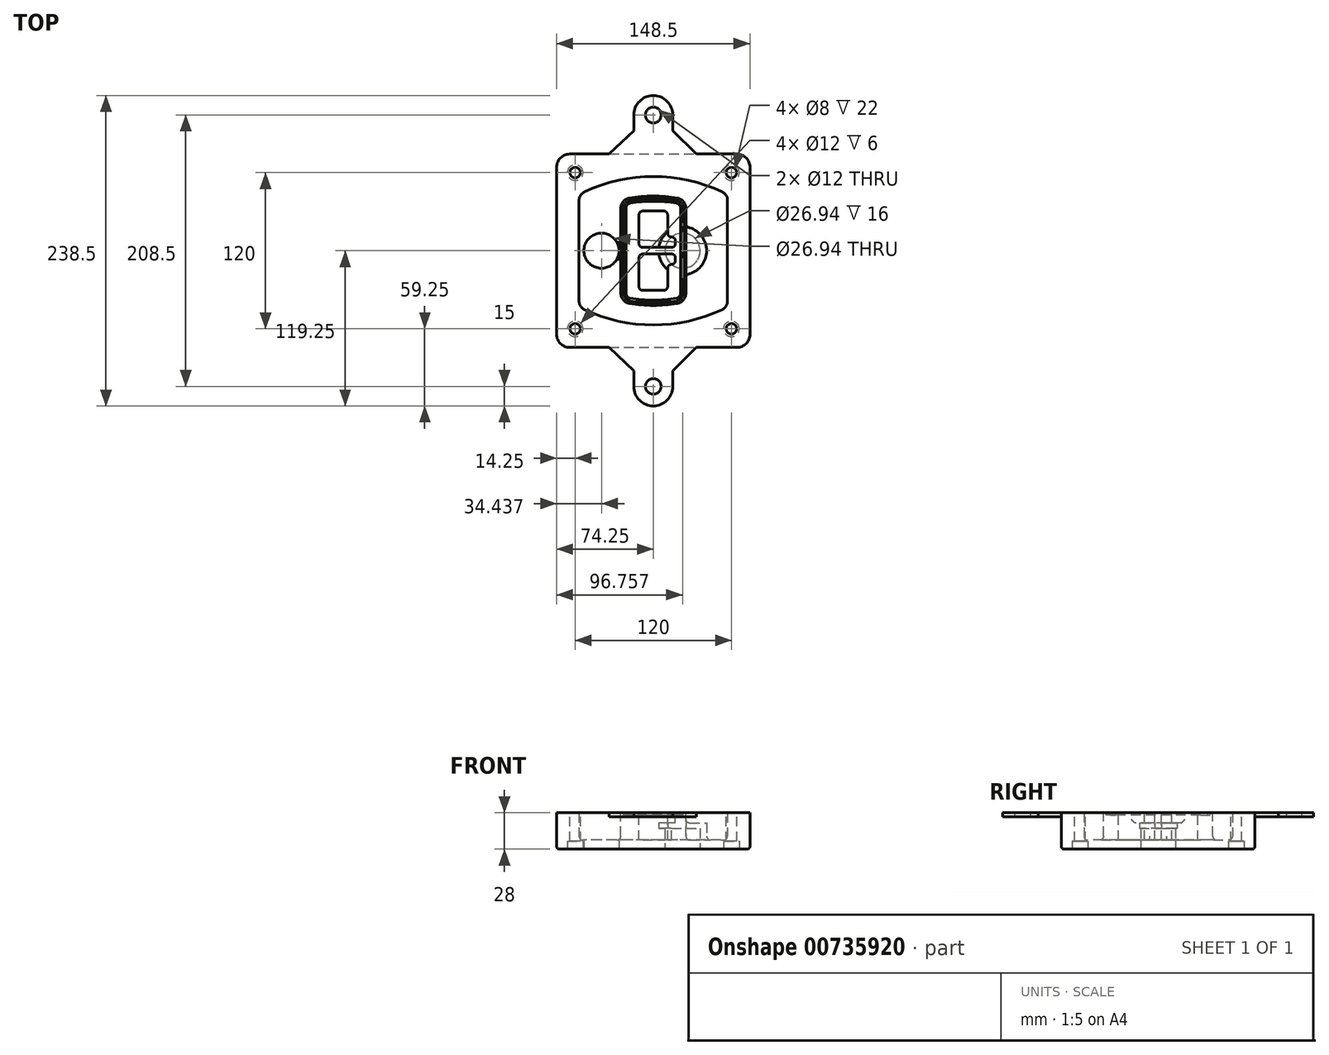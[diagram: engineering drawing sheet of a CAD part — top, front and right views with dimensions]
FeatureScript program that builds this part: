
annotation { "Feature Type Name" : "Feature", "Feature Type Description" : "" }
export const myFeature = defineFeature(function(context is Context, id is Id, definition is map)
    precondition{}
    {
        {
            var Q0;
            Q0=qCreatedBy(makeId("Top.planeOp"),FACE);
            var sketch = newSketch(context, id + "F0", { "sketchPlane" : qUnion([Q0])});
            skPoint(sketch, "E0.rect.middle", {"position": v(0, 0) * mm});
            skLineSegment(sketch, "E1.bottom", {"start": v(-64.25, -74.25) * mm, "end": v(64.25, -74.25) * mm});
            skLineSegment(sketch, "E1.top", {"start": v(-64.25, 74.25) * mm, "end": v(64.25, 74.25) * mm});
            skLineSegment(sketch, "E1.left", {"start": v(-74.25, -64.25) * mm, "end": v(-74.25, 64.25) * mm});
            skLineSegment(sketch, "E1.right", {"start": v(74.25, -64.25) * mm, "end": v(74.25, 64.25) * mm});
            skLineSegment(sketch, "E2", {"start": v(-74.25, 74.25) * mm, "end": v(74.25, -74.25) * mm, "construction": true});
            skLineSegment(sketch, "E3", {"start": v(74.25, 74.25) * mm, "end": v(-74.25, -74.25) * mm, "construction": true});
            skCircle(sketch, "E4", {"center": v(-60, 60) * mm, "radius": 4 * mm});
            skCircle(sketch, "E5", {"center": v(60, 60) * mm, "radius": 4 * mm});
            skCircle(sketch, "E6", {"center": v(60, -60) * mm, "radius": 4 * mm});
            skCircle(sketch, "E7", {"center": v(-60, -60) * mm, "radius": 4 * mm});
            skLineSegment(sketch, "E8", {"start": v(-60, 60) * mm, "end": v(60, 60) * mm, "construction": true});
            skLineSegment(sketch, "E9", {"start": v(60, 60) * mm, "end": v(60, -60) * mm, "construction": true});
            skLineSegment(sketch, "E10", {"start": v(60, -60) * mm, "end": v(-60, -60) * mm, "construction": true});
            skLineSegment(sketch, "E11", {"start": v(-60, -60) * mm, "end": v(-60, 60) * mm, "construction": true});
            skLineSegment(sketch, "E12", {"start": v(-60, 38.83) * mm, "end": v(-60, -38.83) * mm});
            skLineSegment(sketch, "E13", {"start": v(60, 38.83) * mm, "end": v(60, -38.83) * mm});
            skArc(sketch, "E14", {"start": v(54.26, 47.88) * mm, "mid": v(0, 60) * mm, "end": v(-54.26, 47.88) * mm});
            skArc(sketch, "E15", {"start": v(-54.26, -47.88) * mm, "mid": v(0, -60) * mm, "end": v(54.26, -47.88) * mm});
            skLineSegment(sketch, "E16", {"start": v(-60, 0) * mm, "end": v(60, 0) * mm, "construction": true});
            skPoint(sketch, "E17.visualSharp", {"position": v(-60, -45) * mm});
            skArc(sketch, "E17.filletArc", {"start": v(-60, -38.83) * mm, "mid": v(-58.44, -44.2) * mm, "end": v(-54.26, -47.88) * mm});
            skPoint(sketch, "E18.visualSharp", {"position": v(-60, 45) * mm});
            skArc(sketch, "E18.filletArc", {"start": v(-54.26, 47.88) * mm, "mid": v(-58.44, 44.2) * mm, "end": v(-60, 38.83) * mm});
            skPoint(sketch, "E19.visualSharp", {"position": v(60, 45) * mm});
            skArc(sketch, "E19.filletArc", {"start": v(60, 38.83) * mm, "mid": v(58.44, 44.2) * mm, "end": v(54.26, 47.88) * mm});
            skPoint(sketch, "E20.visualSharp", {"position": v(60, -45) * mm});
            skArc(sketch, "E20.filletArc", {"start": v(54.26, -47.88) * mm, "mid": v(58.44, -44.2) * mm, "end": v(60, -38.83) * mm});
            skPoint(sketch, "E21.visualSharp", {"position": v(-74.25, 74.25) * mm});
            skArc(sketch, "E21.filletArc", {"start": v(-64.25, 74.25) * mm, "mid": v(-71.32, 71.32) * mm, "end": v(-74.25, 64.25) * mm});
            skPoint(sketch, "E22.visualSharp", {"position": v(74.25, 74.25) * mm});
            skArc(sketch, "E22.filletArc", {"start": v(74.25, 64.25) * mm, "mid": v(71.32, 71.32) * mm, "end": v(64.25, 74.25) * mm});
            skPoint(sketch, "E23.visualSharp", {"position": v(74.25, -74.25) * mm});
            skArc(sketch, "E23.filletArc", {"start": v(64.25, -74.25) * mm, "mid": v(71.32, -71.32) * mm, "end": v(74.25, -64.25) * mm});
            skPoint(sketch, "E24.visualSharp", {"position": v(-74.25, -74.25) * mm});
            skArc(sketch, "E24.filletArc", {"start": v(-74.25, -64.25) * mm, "mid": v(-71.32, -71.32) * mm, "end": v(-64.25, -74.25) * mm});
            skArc(sketch, "E25.0", {"start": v(57, 38.83) * mm, "mid": v(55.9, 42.58) * mm, "end": v(52.98, 45.17) * mm});
            skLineSegment(sketch, "E25.1", {"start": v(57, 38.83) * mm, "end": v(57, -38.83) * mm});
            skArc(sketch, "E25.2", {"start": v(52.98, -45.17) * mm, "mid": v(55.9, -42.58) * mm, "end": v(57, -38.83) * mm});
            skArc(sketch, "E25.3", {"start": v(-52.98, -45.17) * mm, "mid": v(0, -57) * mm, "end": v(52.98, -45.17) * mm});
            skArc(sketch, "E25.4", {"start": v(-57, -38.83) * mm, "mid": v(-55.9, -42.58) * mm, "end": v(-52.98, -45.17) * mm});
            skArc(sketch, "E25.5", {"start": v(52.98, 45.17) * mm, "mid": v(0, 57) * mm, "end": v(-52.98, 45.17) * mm});
            skLineSegment(sketch, "E25.6", {"start": v(-57, 38.83) * mm, "end": v(-57, -38.83) * mm});
            skArc(sketch, "E25.7", {"start": v(-52.98, 45.17) * mm, "mid": v(-55.9, 42.58) * mm, "end": v(-57, 38.83) * mm});
            skArc(sketch, "E26.0", {"start": v(-55.96, 51.5) * mm, "mid": v(-61.82, 46.33) * mm, "end": v(-64, 38.83) * mm});
            skArc(sketch, "E26.1", {"start": v(55.96, 51.5) * mm, "mid": v(0, 64) * mm, "end": v(-55.96, 51.5) * mm});
            skArc(sketch, "E26.2", {"start": v(64, 38.83) * mm, "mid": v(61.82, 46.33) * mm, "end": v(55.96, 51.5) * mm});
            skLineSegment(sketch, "E26.3", {"start": v(64, 38.83) * mm, "end": v(64, -38.83) * mm});
            skArc(sketch, "E26.4", {"start": v(55.96, -51.5) * mm, "mid": v(61.82, -46.33) * mm, "end": v(64, -38.83) * mm});
            skLineSegment(sketch, "E26.5", {"start": v(-64, 38.83) * mm, "end": v(-64, -38.83) * mm});
            skArc(sketch, "E26.6", {"start": v(-55.96, -51.5) * mm, "mid": v(0, -64) * mm, "end": v(55.96, -51.5) * mm});
            skArc(sketch, "E26.7", {"start": v(-64, -38.83) * mm, "mid": v(-61.82, -46.33) * mm, "end": v(-55.96, -51.5) * mm});
            skSolve(sketch);
        }
        {
            var Q0;
            Q0=makeQuery(id+"F0.imprint","IMPRINT",FACE,{"disambiguationData":[TD([[makeQuery(id+"F0.imprint","IMPRINT",EDGE,{"derivedFrom":sQuery(id+"F0.wireOp",EDGE,"E1.bottom")}),1.0]])]});
            var Q1;
            Q1=makeQuery(id+"F0.imprint","IMPRINT",FACE,{"disambiguationData":[TD([[makeQuery(id+"F0.imprint","IMPRINT",EDGE,{"derivedFrom":sQuery(id+"F0.wireOp",EDGE,"E12")}),1.0]])]});
            var Q2;
            Q2=makeQuery(id+"F0.imprint","IMPRINT",FACE,{"disambiguationData":[TD([[makeQuery(id+"F0.imprint","IMPRINT",EDGE,{"derivedFrom":sQuery(id+"F0.wireOp",EDGE,"E25.0")}),1.0]])]});
            var Q3;
            Q3=makeQuery(id+"F0.imprint","IMPRINT",FACE,{"disambiguationData":[TD([[makeQuery(id+"F0.imprint","IMPRINT",EDGE,{"derivedFrom":sQuery(id+"F0.wireOp",EDGE,"E12")}),-1.0]])]});
            extrude(context, id + "F1", {"entities" : qUnion([Q0, Q1, Q2, Q3]), "oppositeDirection" : true, "depth" : 25 * mm});
        }
        {
            var Q0;
            Q0=makeQuery(id+"F0.imprint","IMPRINT",FACE,{"disambiguationData":[TD([[makeQuery(id+"F0.imprint","IMPRINT",EDGE,{"derivedFrom":sQuery(id+"F0.wireOp",EDGE,"E12")}),1.0]])]});
            extrude(context, id + "F2", {"entities" : qUnion([Q0]), "operationType" : NewBodyOperationType.ADD, "depth" : 3 * mm});
        }
        {
            var Q0;
            Q0=makeQuery(id+"F0.imprint","IMPRINT",FACE,{"disambiguationData":[TD([[makeQuery(id+"F0.imprint","IMPRINT",EDGE,{"derivedFrom":sQuery(id+"F0.wireOp",EDGE,"E25.0")}),1.0]])]});
            extrude(context, id + "F3", {"entities" : qUnion([Q0]), "operationType" : NewBodyOperationType.REMOVE, "oppositeDirection" : true, "depth" : 18 * mm});
        }
        {
            var Q0;
            Q0=makeQuery(id+"F2.opExtrude","CAP_FACE",FACE,{"disambiguationData":[OSD([sQuery(id+"F0.wireOp",EDGE,"E12"),sQuery(id+"F0.wireOp",EDGE,"E13"),sQuery(id+"F0.wireOp",EDGE,"E14"),sQuery(id+"F0.wireOp",EDGE,"E15"),sQuery(id+"F0.wireOp",EDGE,"E17.filletArc"),sQuery(id+"F0.wireOp",EDGE,"E18.filletArc"),sQuery(id+"F0.wireOp",EDGE,"E19.filletArc"),sQuery(id+"F0.wireOp",EDGE,"E20.filletArc"),sQuery(id+"F0.wireOp",EDGE,"E25.0"),sQuery(id+"F0.wireOp",EDGE,"E25.1"),sQuery(id+"F0.wireOp",EDGE,"E25.2"),sQuery(id+"F0.wireOp",EDGE,"E25.3"),sQuery(id+"F0.wireOp",EDGE,"E25.4"),sQuery(id+"F0.wireOp",EDGE,"E25.5"),sQuery(id+"F0.wireOp",EDGE,"E25.6"),sQuery(id+"F0.wireOp",EDGE,"E25.7")])],"isStart":false});
            var sketch = newSketch(context, id + "F4", { "sketchPlane" : qUnion([Q0])});
            skArc(sketch, "E27.0", {"start": v(-18.34, -40.45) * mm, "mid": v(0, -42) * mm, "end": v(18.34, -40.45) * mm});
            skArc(sketch, "E28.0", {"start": v(18.34, 40.45) * mm, "mid": v(0, 42) * mm, "end": v(-18.34, 40.45) * mm});
            skLineSegment(sketch, "E29", {"start": v(-25, 32.57) * mm, "end": v(-25, -32.57) * mm});
            skLineSegment(sketch, "E30", {"start": v(25, 32.57) * mm, "end": v(25, -32.57) * mm});
            skLineSegment(sketch, "E31", {"start": v(-25, 39.1) * mm, "end": v(25, 39.1) * mm, "construction": true});
            skLineSegment(sketch, "E32", {"start": v(-25, -39.1) * mm, "end": v(25, -39.1) * mm, "construction": true});
            skPoint(sketch, "E33.visualSharp", {"position": v(-25, 39.1) * mm});
            skArc(sketch, "E33.filletArc", {"start": v(-18.34, 40.45) * mm, "mid": v(-23.11, 37.73) * mm, "end": v(-25, 32.57) * mm});
            skPoint(sketch, "E34.visualSharp", {"position": v(25, 39.1) * mm});
            skArc(sketch, "E34.filletArc", {"start": v(25, 32.57) * mm, "mid": v(23.11, 37.73) * mm, "end": v(18.34, 40.45) * mm});
            skPoint(sketch, "E35.visualSharp", {"position": v(25, -39.1) * mm});
            skArc(sketch, "E35.filletArc", {"start": v(18.34, -40.45) * mm, "mid": v(23.11, -37.73) * mm, "end": v(25, -32.57) * mm});
            skPoint(sketch, "E36.visualSharp", {"position": v(-25, -39.1) * mm});
            skArc(sketch, "E36.filletArc", {"start": v(-25, -32.57) * mm, "mid": v(-23.11, -37.73) * mm, "end": v(-18.34, -40.45) * mm});
            skArc(sketch, "E37.0", {"start": v(52.98, 45.17) * mm, "mid": v(0, 57) * mm, "end": v(-52.98, 45.17) * mm});
            skArc(sketch, "E37.1", {"start": v(-52.98, 45.17) * mm, "mid": v(-55.9, 42.58) * mm, "end": v(-57, 38.83) * mm});
            skLineSegment(sketch, "E37.2", {"start": v(-57, 38.83) * mm, "end": v(-57, -38.83) * mm});
            skArc(sketch, "E37.3", {"start": v(-57, -38.83) * mm, "mid": v(-55.9, -42.58) * mm, "end": v(-52.98, -45.17) * mm});
            skArc(sketch, "E37.4", {"start": v(-52.98, -45.17) * mm, "mid": v(0, -57) * mm, "end": v(52.98, -45.17) * mm});
            skArc(sketch, "E37.5", {"start": v(52.98, -45.17) * mm, "mid": v(55.9, -42.58) * mm, "end": v(57, -38.83) * mm});
            skLineSegment(sketch, "E37.6", {"start": v(57, 38.83) * mm, "end": v(57, -38.83) * mm});
            skArc(sketch, "E37.7", {"start": v(57, 38.83) * mm, "mid": v(55.9, 42.58) * mm, "end": v(52.98, 45.17) * mm});
            skLineSegment(sketch, "E38.0", {"start": v(23, 32.57) * mm, "end": v(23, -32.57) * mm});
            skArc(sketch, "E38.1", {"start": v(18, -38.48) * mm, "mid": v(21.58, -36.44) * mm, "end": v(23, -32.57) * mm});
            skArc(sketch, "E38.2", {"start": v(-18, -38.48) * mm, "mid": v(0, -40) * mm, "end": v(18, -38.48) * mm});
            skArc(sketch, "E38.3", {"start": v(-23, -32.57) * mm, "mid": v(-21.58, -36.44) * mm, "end": v(-18, -38.48) * mm});
            skLineSegment(sketch, "E38.4", {"start": v(-23, 32.57) * mm, "end": v(-23, -32.57) * mm});
            skArc(sketch, "E38.5", {"start": v(23, 32.57) * mm, "mid": v(21.58, 36.44) * mm, "end": v(18, 38.48) * mm});
            skArc(sketch, "E38.6", {"start": v(-18, 38.48) * mm, "mid": v(-21.58, 36.44) * mm, "end": v(-23, 32.57) * mm});
            skArc(sketch, "E38.7", {"start": v(18, 38.48) * mm, "mid": v(0, 40) * mm, "end": v(-18, 38.48) * mm});
            skArc(sketch, "E39.0", {"start": v(21, 32.57) * mm, "mid": v(20.06, 35.15) * mm, "end": v(17.67, 36.5) * mm});
            skLineSegment(sketch, "E39.1", {"start": v(21, 32.57) * mm, "end": v(21, -32.57) * mm});
            skArc(sketch, "E39.2", {"start": v(17.67, -36.5) * mm, "mid": v(20.06, -35.15) * mm, "end": v(21, -32.57) * mm});
            skArc(sketch, "E39.3", {"start": v(-17.67, -36.5) * mm, "mid": v(0, -38) * mm, "end": v(17.67, -36.5) * mm});
            skArc(sketch, "E39.4", {"start": v(-21, -32.57) * mm, "mid": v(-20.06, -35.15) * mm, "end": v(-17.67, -36.5) * mm});
            skArc(sketch, "E39.5", {"start": v(17.67, 36.5) * mm, "mid": v(0, 38) * mm, "end": v(-17.67, 36.5) * mm});
            skLineSegment(sketch, "E39.6", {"start": v(-21, 32.57) * mm, "end": v(-21, -32.57) * mm});
            skArc(sketch, "E39.7", {"start": v(-17.67, 36.5) * mm, "mid": v(-20.06, 35.15) * mm, "end": v(-21, 32.57) * mm});
            skLineSegment(sketch, "E40", {"start": v(-25, 0) * mm, "end": v(25, 0) * mm, "construction": true});
            skLineSegment(sketch, "E41", {"start": v(-11, 5.5) * mm, "end": v(-11, 27.5) * mm});
            skLineSegment(sketch, "E42", {"start": v(-8, 30.5) * mm, "end": v(8, 30.5) * mm});
            skLineSegment(sketch, "E43", {"start": v(11, 27.5) * mm, "end": v(11, 13.5) * mm});
            skLineSegment(sketch, "E44", {"start": v(14, 10.5) * mm, "end": v(14, 10.5) * mm});
            skLineSegment(sketch, "E45", {"start": v(17, 7.5) * mm, "end": v(17, 5.5) * mm});
            skLineSegment(sketch, "E46", {"start": v(14, 2.5) * mm, "end": v(-8, 2.5) * mm});
            skPoint(sketch, "E47.visualSharp", {"position": v(-11, 30.5) * mm});
            skArc(sketch, "E47.filletArc", {"start": v(-8, 30.5) * mm, "mid": v(-10.12, 29.62) * mm, "end": v(-11, 27.5) * mm});
            skPoint(sketch, "E48.visualSharp", {"position": v(11, 30.5) * mm});
            skArc(sketch, "E48.filletArc", {"start": v(11, 27.5) * mm, "mid": v(10.12, 29.62) * mm, "end": v(8, 30.5) * mm});
            skPoint(sketch, "E49.visualSharp", {"position": v(11, 10.5) * mm});
            skArc(sketch, "E49.filletArc", {"start": v(11, 13.5) * mm, "mid": v(11.88, 11.38) * mm, "end": v(14, 10.5) * mm});
            skPoint(sketch, "E50.visualSharp", {"position": v(17, 10.5) * mm});
            skArc(sketch, "E50.filletArc", {"start": v(17, 7.5) * mm, "mid": v(16.12, 9.62) * mm, "end": v(14, 10.5) * mm});
            skPoint(sketch, "E51.visualSharp", {"position": v(17, 2.5) * mm});
            skArc(sketch, "E51.filletArc", {"start": v(14, 2.5) * mm, "mid": v(16.12, 3.38) * mm, "end": v(17, 5.5) * mm});
            skPoint(sketch, "E52.visualSharp", {"position": v(-11, 2.5) * mm});
            skArc(sketch, "E52.filletArc", {"start": v(-11, 5.5) * mm, "mid": v(-10.12, 3.38) * mm, "end": v(-8, 2.5) * mm});
            skLineSegment(sketch, "E53.0.MirrorCS", {"start": v(14, -2.5) * mm, "end": v(-8, -2.5) * mm});
            skArc(sketch, "E54.0.MirrorCS", {"start": v(-11, -5.5) * mm, "mid": v(-10.12, -3.38) * mm, "end": v(-8, -2.5) * mm});
            skLineSegment(sketch, "E55.0.MirrorCS", {"start": v(-11, -5.5) * mm, "end": v(-11, -27.5) * mm});
            skArc(sketch, "E56.0.MirrorCS", {"start": v(-8, -30.5) * mm, "mid": v(-10.12, -29.62) * mm, "end": v(-11, -27.5) * mm});
            skLineSegment(sketch, "E57.0.MirrorCS", {"start": v(-8, -30.5) * mm, "end": v(8, -30.5) * mm});
            skArc(sketch, "E58.0.MirrorCS", {"start": v(11, -27.5) * mm, "mid": v(10.12, -29.62) * mm, "end": v(8, -30.5) * mm});
            skLineSegment(sketch, "E59.0.MirrorCS", {"start": v(11, -27.5) * mm, "end": v(11, -13.5) * mm});
            skArc(sketch, "E60.0.MirrorCS", {"start": v(11, -13.5) * mm, "mid": v(11.88, -11.38) * mm, "end": v(14, -10.5) * mm});
            skArc(sketch, "E61.0.MirrorCS", {"start": v(17, -7.5) * mm, "mid": v(16.12, -9.62) * mm, "end": v(14, -10.5) * mm});
            skLineSegment(sketch, "E62.0.MirrorCS", {"start": v(17, -7.5) * mm, "end": v(17, -5.5) * mm});
            skArc(sketch, "E63.0.MirrorCS", {"start": v(14, -2.5) * mm, "mid": v(16.12, -3.38) * mm, "end": v(17, -5.5) * mm});
            skSolve(sketch);
        }
        {
            var Q0;
            Q0=makeQuery(id+"F4.imprint","IMPRINT",FACE,{"disambiguationData":[TD([[makeQuery(id+"F4.imprint","IMPRINT",EDGE,{"derivedFrom":sQuery(id+"F4.wireOp",EDGE,"E27.0")}),1.0]])]});
            var Q1;
            Q1=makeQuery(id+"F4.imprint","IMPRINT",FACE,{"disambiguationData":[TD([[makeQuery(id+"F4.imprint","IMPRINT",EDGE,{"derivedFrom":sQuery(id+"F4.wireOp",EDGE,"E38.0")}),-1.0]])]});
            var Q2;
            Q2=makeQuery(id+"F4.imprint","IMPRINT",FACE,{"disambiguationData":[TD([[makeQuery(id+"F4.imprint","IMPRINT",EDGE,{"derivedFrom":sQuery(id+"F4.wireOp",EDGE,"E39.0")}),1.0]])]});
            extrude(context, id + "F5", {"entities" : qUnion([Q0, Q1, Q2]), "operationType" : NewBodyOperationType.ADD, "endBound" : BoundingType.UP_TO_NEXT, "oppositeDirection" : true, "depth" : 25 * mm});
        }
        {
            var Q0;
            Q0=makeQuery(id+"F4.imprint","IMPRINT",FACE,{"disambiguationData":[TD([[makeQuery(id+"F4.imprint","IMPRINT",EDGE,{"derivedFrom":sQuery(id+"F4.wireOp",EDGE,"E38.0")}),-1.0]])]});
            extrude(context, id + "F6", {"entities" : qUnion([Q0]), "operationType" : NewBodyOperationType.REMOVE, "oppositeDirection" : true, "depth" : 2 * mm});
        }
        {
            var Q0;
            Q0=makeQuery(id+"F1.opExtrude","CAP_FACE",FACE,{"disambiguationData":[OSD([sQuery(id+"F0.wireOp",EDGE,"E1.bottom"),sQuery(id+"F0.wireOp",EDGE,"E1.top"),sQuery(id+"F0.wireOp",EDGE,"E1.left"),sQuery(id+"F0.wireOp",EDGE,"E1.right"),sQuery(id+"F0.wireOp",EDGE,"E4"),sQuery(id+"F0.wireOp",EDGE,"E5"),sQuery(id+"F0.wireOp",EDGE,"E6"),sQuery(id+"F0.wireOp",EDGE,"E7"),sQuery(id+"F0.wireOp",EDGE,"E21.filletArc"),sQuery(id+"F0.wireOp",EDGE,"E22.filletArc"),sQuery(id+"F0.wireOp",EDGE,"E23.filletArc"),sQuery(id+"F0.wireOp",EDGE,"E24.filletArc")])],"isStart":false});
            var sketch = newSketch(context, id + "F7", { "sketchPlane" : qUnion([Q0])});
            skCircle(sketch, "E64", {"center": v(22.5, 0) * mm, "radius": 13.47 * mm});
            skCircle(sketch, "E65", {"center": v(-39.81, 0) * mm, "radius": 13.47 * mm});
            skLineSegment(sketch, "E66", {"start": v(74.25, 0) * mm, "end": v(-74.25, 0) * mm});
            skCircle(sketch, "E67", {"center": v(22.5, 0) * mm, "radius": 18.47 * mm});
            skCircle(sketch, "E68", {"center": v(60, -60) * mm, "radius": 6 * mm});
            skCircle(sketch, "E69", {"center": v(-60, -60) * mm, "radius": 6 * mm});
            skCircle(sketch, "E70", {"center": v(-60, 60) * mm, "radius": 6 * mm});
            skCircle(sketch, "E71", {"center": v(60, 60) * mm, "radius": 6 * mm});
            skSolve(sketch);
        }
        {
            var Q0;
            {var subQ1=sQuery(id+"F7.wireOp",EDGE,"E66");var subQ4=sQuery(id+"F7.wireOp",EDGE,"E64");var subQ6=makeQuery(id+"F7.imprint","INTERSECT",VERTEX,{"disambiguationData":[OD(0.0)],"derivedFrom":[subQ4,subQ1]});Q0=makeQuery(id+"F7.imprint","IMPRINT",FACE,{"disambiguationData":[TD([[makeQuery(id+"F7.imprint","IMPRINT",EDGE,{"disambiguationData":[TD([[subQ6,-1.0]])],"derivedFrom":subQ4}),-1.0]])]});}
            var Q1;
            {var subQ0=sQuery(id+"F7.wireOp",EDGE,"E66");var subQ1=sQuery(id+"F7.wireOp",EDGE,"E64");var subQ3=makeQuery(id+"F7.imprint","INTERSECT",VERTEX,{"disambiguationData":[OD(0.0)],"derivedFrom":[subQ1,subQ0]});Q1=makeQuery(id+"F7.imprint","IMPRINT",FACE,{"disambiguationData":[TD([[makeQuery(id+"F7.imprint","IMPRINT",EDGE,{"disambiguationData":[TD([[subQ3,-1.0]])],"derivedFrom":subQ1}),1.0]])]});}
            var Q2;
            {var subQ0=sQuery(id+"F7.wireOp",EDGE,"E66");var subQ1=sQuery(id+"F7.wireOp",EDGE,"E64");var subQ3=makeQuery(id+"F7.imprint","INTERSECT",VERTEX,{"disambiguationData":[OD(0.0)],"derivedFrom":[subQ1,subQ0]});Q2=makeQuery(id+"F7.imprint","IMPRINT",FACE,{"disambiguationData":[TD([[makeQuery(id+"F7.imprint","IMPRINT",EDGE,{"disambiguationData":[TD([[subQ3,1.0]])],"derivedFrom":subQ1}),1.0]])]});}
            var Q3;
            {var subQ1=sQuery(id+"F7.wireOp",EDGE,"E66");var subQ4=sQuery(id+"F7.wireOp",EDGE,"E64");var subQ6=makeQuery(id+"F7.imprint","INTERSECT",VERTEX,{"disambiguationData":[OD(0.0)],"derivedFrom":[subQ4,subQ1]});Q3=makeQuery(id+"F7.imprint","IMPRINT",FACE,{"disambiguationData":[TD([[makeQuery(id+"F7.imprint","IMPRINT",EDGE,{"disambiguationData":[TD([[subQ6,1.0]])],"derivedFrom":subQ4}),-1.0]])]});}
            extrude(context, id + "F8", {"entities" : qUnion([Q0, Q1, Q2, Q3]), "operationType" : NewBodyOperationType.ADD, "oppositeDirection" : true, "depth" : 20 * mm});
        }
        {
            var Q0;
            {var subQ0=sQuery(id+"F7.wireOp",EDGE,"E66");var subQ1=sQuery(id+"F7.wireOp",EDGE,"E64");var subQ3=makeQuery(id+"F7.imprint","INTERSECT",VERTEX,{"disambiguationData":[OD(0.0)],"derivedFrom":[subQ1,subQ0]});Q0=makeQuery(id+"F7.imprint","IMPRINT",FACE,{"disambiguationData":[TD([[makeQuery(id+"F7.imprint","IMPRINT",EDGE,{"disambiguationData":[TD([[subQ3,-1.0]])],"derivedFrom":subQ1}),1.0]])]});}
            var Q1;
            {var subQ0=sQuery(id+"F7.wireOp",EDGE,"E66");var subQ1=sQuery(id+"F7.wireOp",EDGE,"E64");var subQ3=makeQuery(id+"F7.imprint","INTERSECT",VERTEX,{"disambiguationData":[OD(0.0)],"derivedFrom":[subQ1,subQ0]});Q1=makeQuery(id+"F7.imprint","IMPRINT",FACE,{"disambiguationData":[TD([[makeQuery(id+"F7.imprint","IMPRINT",EDGE,{"disambiguationData":[TD([[subQ3,1.0]])],"derivedFrom":subQ1}),1.0]])]});}
            extrude(context, id + "F9", {"entities" : qUnion([Q0, Q1]), "operationType" : NewBodyOperationType.REMOVE, "oppositeDirection" : true, "depth" : 16 * mm});
        }
        {
            var Q0;
            {var subQ0=sQuery(id+"F7.wireOp",EDGE,"E66");var subQ1=sQuery(id+"F7.wireOp",EDGE,"E65");var subQ3=makeQuery(id+"F7.imprint","INTERSECT",VERTEX,{"disambiguationData":[OD(0.0)],"derivedFrom":[subQ1,subQ0]});Q0=makeQuery(id+"F7.imprint","IMPRINT",FACE,{"disambiguationData":[TD([[makeQuery(id+"F7.imprint","IMPRINT",EDGE,{"disambiguationData":[TD([[subQ3,-1.0]])],"derivedFrom":subQ1}),1.0]])]});}
            var Q1;
            {var subQ0=sQuery(id+"F7.wireOp",EDGE,"E66");var subQ1=sQuery(id+"F7.wireOp",EDGE,"E65");var subQ3=makeQuery(id+"F7.imprint","INTERSECT",VERTEX,{"disambiguationData":[OD(0.0)],"derivedFrom":[subQ1,subQ0]});Q1=makeQuery(id+"F7.imprint","IMPRINT",FACE,{"disambiguationData":[TD([[makeQuery(id+"F7.imprint","IMPRINT",EDGE,{"disambiguationData":[TD([[subQ3,1.0]])],"derivedFrom":subQ1}),1.0]])]});}
            extrude(context, id + "F10", {"entities" : qUnion([Q0, Q1]), "operationType" : NewBodyOperationType.REMOVE, "oppositeDirection" : true, "depth" : 25 * mm});
        }
        {
            var Q0;
            Q0=makeQuery(id+"F7.imprint","IMPRINT",FACE,{"disambiguationData":[TD([[makeQuery(id+"F7.imprint","IMPRINT",EDGE,{"derivedFrom":sQuery(id+"F7.wireOp",EDGE,"E68")}),1.0]])]});
            var Q1;
            Q1=makeQuery(id+"F7.imprint","IMPRINT",FACE,{"disambiguationData":[TD([[makeQuery(id+"F7.imprint","IMPRINT",EDGE,{"derivedFrom":makeQuery(id+"F1.opExtrude","CAP_EDGE",EDGE,{"disambiguationData":[OSD([sQuery(id+"F0.wireOp",EDGE,"E5")])],"isStart":false})}),-1.0]])]});
            var Q2;
            Q2=makeQuery(id+"F7.imprint","IMPRINT",FACE,{"disambiguationData":[TD([[makeQuery(id+"F7.imprint","IMPRINT",EDGE,{"derivedFrom":sQuery(id+"F7.wireOp",EDGE,"E69")}),1.0]])]});
            var Q3;
            Q3=makeQuery(id+"F7.imprint","IMPRINT",FACE,{"disambiguationData":[TD([[makeQuery(id+"F7.imprint","IMPRINT",EDGE,{"derivedFrom":makeQuery(id+"F1.opExtrude","CAP_EDGE",EDGE,{"disambiguationData":[OSD([sQuery(id+"F0.wireOp",EDGE,"E4")])],"isStart":false})}),-1.0]])]});
            var Q4;
            Q4=makeQuery(id+"F7.imprint","IMPRINT",FACE,{"disambiguationData":[TD([[makeQuery(id+"F7.imprint","IMPRINT",EDGE,{"derivedFrom":sQuery(id+"F7.wireOp",EDGE,"E70")}),1.0]])]});
            var Q5;
            Q5=makeQuery(id+"F7.imprint","IMPRINT",FACE,{"disambiguationData":[TD([[makeQuery(id+"F7.imprint","IMPRINT",EDGE,{"derivedFrom":makeQuery(id+"F1.opExtrude","CAP_EDGE",EDGE,{"disambiguationData":[OSD([sQuery(id+"F0.wireOp",EDGE,"E7")])],"isStart":false})}),-1.0]])]});
            var Q6;
            Q6=makeQuery(id+"F7.imprint","IMPRINT",FACE,{"disambiguationData":[TD([[makeQuery(id+"F7.imprint","IMPRINT",EDGE,{"derivedFrom":sQuery(id+"F7.wireOp",EDGE,"E71")}),1.0]])]});
            var Q7;
            Q7=makeQuery(id+"F7.imprint","IMPRINT",FACE,{"disambiguationData":[TD([[makeQuery(id+"F7.imprint","IMPRINT",EDGE,{"derivedFrom":makeQuery(id+"F1.opExtrude","CAP_EDGE",EDGE,{"disambiguationData":[OSD([sQuery(id+"F0.wireOp",EDGE,"E6")])],"isStart":false})}),-1.0]])]});
            extrude(context, id + "F11", {"entities" : qUnion([Q0, Q1, Q2, Q3, Q4, Q5, Q6, Q7]), "operationType" : NewBodyOperationType.REMOVE, "oppositeDirection" : true, "depth" : 6 * mm});
        }
        {
            var Q0;
            Q0=makeQuery(id+"F9.boolean.opBoolean","COPY",FACE,{"derivedFrom":makeQuery(id+"F9.opExtrude","CAP_FACE",FACE,{"disambiguationData":[OSD([sQuery(id+"F7.wireOp",EDGE,"E64")])],"isStart":false})});
            var sketch = newSketch(context, id + "F12", { "sketchPlane" : qUnion([Q0])});
            skArc(sketch, "E72.0", {"start": v(11, 14.45) * mm, "mid": v(6.45, 9.13) * mm, "end": v(4.2, 2.5) * mm});
            skArc(sketch, "E72.1", {"start": v(4.2, -2.5) * mm, "mid": v(6.45, -9.13) * mm, "end": v(11, -14.45) * mm});
            skLineSegment(sketch, "E73", {"start": v(4.2, -2.5) * mm, "end": v(14, -2.5) * mm});
            skLineSegment(sketch, "E74.0", {"start": v(14, 2.5) * mm, "end": v(4.2, 2.5) * mm});
            skArc(sketch, "E74.1", {"start": v(14, 2.5) * mm, "mid": v(16.12, 3.38) * mm, "end": v(17, 5.5) * mm});
            skLineSegment(sketch, "E74.2", {"start": v(17, 7.5) * mm, "end": v(17, 5.5) * mm});
            skArc(sketch, "E74.3", {"start": v(17, 7.5) * mm, "mid": v(16.12, 9.62) * mm, "end": v(14, 10.5) * mm});
            skArc(sketch, "E74.4", {"start": v(11, 13.5) * mm, "mid": v(11.88, 11.38) * mm, "end": v(14, 10.5) * mm});
            skLineSegment(sketch, "E74.5", {"start": v(11, 14.45) * mm, "end": v(11, 13.5) * mm});
            skLineSegment(sketch, "E74.7", {"start": v(14, -2.5) * mm, "end": v(4.2, -2.5) * mm});
            skArc(sketch, "E74.8", {"start": v(14, -2.5) * mm, "mid": v(16.12, -3.38) * mm, "end": v(17, -5.5) * mm});
            skLineSegment(sketch, "E74.9", {"start": v(17, -7.5) * mm, "end": v(17, -5.5) * mm});
            skArc(sketch, "E74.10", {"start": v(17, -7.5) * mm, "mid": v(16.12, -9.62) * mm, "end": v(14, -10.5) * mm});
            skArc(sketch, "E74.11", {"start": v(11, -13.5) * mm, "mid": v(11.88, -11.38) * mm, "end": v(14, -10.5) * mm});
            skLineSegment(sketch, "E74.12", {"start": v(11, -14.45) * mm, "end": v(11, -13.5) * mm});
            skPoint(sketch, "E75.orphan", {"position": v(11, -27.5) * mm});
            skPoint(sketch, "E76.orphan", {"position": v(-8, -2.5) * mm});
            skPoint(sketch, "E77.orphan", {"position": v(-8, 2.5) * mm});
            skPoint(sketch, "E78.orphan", {"position": v(11, 27.5) * mm});
            skSolve(sketch);
        }
        {
            var Q0;
            {var subQ7=sQuery(id+"F12.wireOp",EDGE,"E72.0");var subQ14=sQuery(id+"F12.wireOp",EDGE,"E72.1");var subQ16=sQuery(id+"F12.wireOp",EDGE,"E74.1");var subQ18=sQuery(id+"F12.wireOp",EDGE,"E74.8");Q0=qUnion([makeQuery(id+"F12.imprint","IMPRINT",FACE,{"disambiguationData":[TD([[makeQuery(id+"F12.imprint","IMPRINT",EDGE,{"derivedFrom":subQ7}),1.0]])]}),makeQuery(id+"F12.imprint","IMPRINT",FACE,{"disambiguationData":[TD([[makeQuery(id+"F12.imprint","IMPRINT",EDGE,{"derivedFrom":subQ14}),1.0]])]}),makeQuery(id+"F12.imprint","IMPRINT",FACE,{"disambiguationData":[TD([[makeQuery(id+"F12.imprint","IMPRINT",EDGE,{"derivedFrom":subQ16}),1.0]])]}),makeQuery(id+"F12.imprint","IMPRINT",FACE,{"disambiguationData":[TD([[makeQuery(id+"F12.imprint","IMPRINT",EDGE,{"derivedFrom":subQ18}),-1.0]])]})]);}
            var Q1;
            Q1=makeQuery(id+"F5.boolean.opBoolean","SPLIT",FACE,{"disambiguationData":[TD([makeQuery(id+"F5.opExtrude","SWEPT_FACE",FACE,{"disambiguationData":[OSD([sQuery(id+"F4.wireOp",EDGE,"E41")])]})])],"derivedFrom":makeQuery(id+"F3.boolean.opBoolean","COPY",FACE,{"derivedFrom":makeQuery(id+"F3.opExtrude","CAP_FACE",FACE,{"disambiguationData":[OSD([sQuery(id+"F0.wireOp",EDGE,"E25.0"),sQuery(id+"F0.wireOp",EDGE,"E25.1"),sQuery(id+"F0.wireOp",EDGE,"E25.2"),sQuery(id+"F0.wireOp",EDGE,"E25.3"),sQuery(id+"F0.wireOp",EDGE,"E25.4"),sQuery(id+"F0.wireOp",EDGE,"E25.5"),sQuery(id+"F0.wireOp",EDGE,"E25.6"),sQuery(id+"F0.wireOp",EDGE,"E25.7")])],"isStart":false})})});
            extrude(context, id + "F13", {"entities" : qUnion([Q0]), "operationType" : NewBodyOperationType.REMOVE, "endBound" : BoundingType.UP_TO_SURFACE, "endBoundEntityFace" : qUnion([Q1]), "depth" : 25 * mm});
        }
        {
            var Q0;
            Q0=makeQuery(id+"F3.boolean.opBoolean","COPY",EDGE,{"derivedFrom":makeQuery(id+"F3.opExtrude","CAP_EDGE",EDGE,{"disambiguationData":[OSD([sQuery(id+"F0.wireOp",EDGE,"E25.6")])],"isStart":false})});
            var Q1;
            Q1=makeQuery(id+"F8.boolean.opBoolean","INTERSECT",EDGE,{"derivedFrom":[makeQuery(id+"F5.opExtrude","SWEPT_FACE",FACE,{"disambiguationData":[OSD([sQuery(id+"F4.wireOp",EDGE,"E30")])]}),makeQuery(id+"F8.opExtrude","CAP_FACE",FACE,{"disambiguationData":[OSD([sQuery(id+"F7.wireOp",EDGE,"E67")])],"isStart":false})]});
            var Q2;
            Q2=makeQuery(id+"F8.boolean.opBoolean","INTERSECT",EDGE,{"disambiguationData":[OD(1.0)],"derivedFrom":[makeQuery(id+"F5.opExtrude","SWEPT_FACE",FACE,{"disambiguationData":[OSD([sQuery(id+"F4.wireOp",EDGE,"E30")])]}),makeQuery(id+"F8.opExtrude","SWEPT_FACE",FACE,{"disambiguationData":[OSD([sQuery(id+"F7.wireOp",EDGE,"E67")])]})]});
            var Q3;
            {var subQ0=sQuery(id+"F4.wireOp",EDGE,"E30");Q3=makeQuery(id+"F8.boolean.opBoolean","SPLIT",EDGE,{"disambiguationData":[TD([makeQuery(id+"F5.opExtrude","SWEPT_FACE",FACE,{"disambiguationData":[OSD([sQuery(id+"F4.wireOp",EDGE,"E35.filletArc")])]})])],"derivedFrom":makeQuery(id+"F5.opExtrude","CAP_EDGE",EDGE,{"disambiguationData":[OSD([subQ0])],"isStart":false})});}
            var Q4;
            {var subQ0=sQuery(id+"F0.wireOp",EDGE,"E25.7");var subQ1=sQuery(id+"F0.wireOp",EDGE,"E25.1");var subQ2=sQuery(id+"F0.wireOp",EDGE,"E25.6");var subQ3=sQuery(id+"F0.wireOp",EDGE,"E25.5");var subQ4=sQuery(id+"F0.wireOp",EDGE,"E25.4");var subQ5=sQuery(id+"F0.wireOp",EDGE,"E25.0");var subQ6=sQuery(id+"F0.wireOp",EDGE,"E25.2");var subQ7=sQuery(id+"F0.wireOp",EDGE,"E25.3");Q4=makeQuery(id+"F8.boolean.opBoolean","INTERSECT",EDGE,{"derivedFrom":[makeQuery(id+"F5.boolean.opBoolean","SPLIT",FACE,{"disambiguationData":[TD([makeQuery(id+"F2.opExtrude","SWEPT_FACE",FACE,{"disambiguationData":[OSD([subQ5])]})])],"derivedFrom":makeQuery(id+"F3.boolean.opBoolean","COPY",FACE,{"derivedFrom":makeQuery(id+"F3.opExtrude","CAP_FACE",FACE,{"disambiguationData":[OSD([subQ5,subQ1,subQ6,subQ7,subQ4,subQ3,subQ2,subQ0])],"isStart":false})})}),makeQuery(id+"F8.opExtrude","SWEPT_FACE",FACE,{"disambiguationData":[OSD([sQuery(id+"F7.wireOp",EDGE,"E67")])]})]});}
            var Q5;
            Q5=makeQuery(id+"F8.boolean.opBoolean","INTERSECT",EDGE,{"disambiguationData":[OD(0.0)],"derivedFrom":[makeQuery(id+"F5.opExtrude","SWEPT_FACE",FACE,{"disambiguationData":[OSD([sQuery(id+"F4.wireOp",EDGE,"E30")])]}),makeQuery(id+"F8.opExtrude","SWEPT_FACE",FACE,{"disambiguationData":[OSD([sQuery(id+"F7.wireOp",EDGE,"E67")])]})]});
            fillet(context, id + "F14", {"entities" : qUnion([Q0, Q1, Q2, Q3, Q4, Q5]), "radius" : 3 * mm, "tangentPropagation" : true, "allowEdgeOverflow" : false});
        }
        {
            var Q0;
            Q0=makeQuery(id+"F1.opExtrude","CAP_EDGE",EDGE,{"disambiguationData":[OSD([sQuery(id+"F0.wireOp",EDGE,"E1.bottom")])],"isStart":false});
            fillet(context, id + "F15", {"entities" : qUnion([Q0]), "radius" : 2 * mm, "tangentPropagation" : true, "allowEdgeOverflow" : false});
        }
        {
            var Q0;
            {var subQ0=sQuery(id+"F0.wireOp",EDGE,"E21.filletArc");var subQ1=sQuery(id+"F0.wireOp",EDGE,"E7");var subQ2=sQuery(id+"F0.wireOp",EDGE,"E6");var subQ3=sQuery(id+"F0.wireOp",EDGE,"E5");var subQ4=sQuery(id+"F0.wireOp",EDGE,"E4");var subQ5=sQuery(id+"F0.wireOp",EDGE,"E22.filletArc");var subQ6=sQuery(id+"F0.wireOp",EDGE,"E1.bottom");var subQ7=sQuery(id+"F0.wireOp",EDGE,"E1.right");var subQ8=sQuery(id+"F0.wireOp",EDGE,"E1.top");var subQ9=sQuery(id+"F0.wireOp",EDGE,"E1.left");var subQ10=sQuery(id+"F0.wireOp",EDGE,"E23.filletArc");var subQ11=sQuery(id+"F0.wireOp",EDGE,"E24.filletArc");Q0=makeQuery(id+"F2.boolean.opBoolean","SPLIT",FACE,{"disambiguationData":[TD([makeQuery(id+"F1.opExtrude","SWEPT_FACE",FACE,{"disambiguationData":[OSD([subQ6])]})])],"derivedFrom":makeQuery(id+"F1.opExtrude","CAP_FACE",FACE,{"disambiguationData":[OSD([subQ6,subQ8,subQ9,subQ7,subQ4,subQ3,subQ2,subQ1,subQ0,subQ5,subQ10,subQ11])],"isStart":true})});}
            var sketch = newSketch(context, id + "F16", { "sketchPlane" : qUnion([Q0])});
            skLineSegment(sketch, "E79", {"start": v(-15, 92.25) * mm, "end": v(-15, 104.25) * mm});
            skLineSegment(sketch, "E80", {"start": v(15, 92.25) * mm, "end": v(15, 104.25) * mm});
            skArc(sketch, "E81", {"start": v(15, 104.25) * mm, "mid": v(0, 119.25) * mm, "end": v(-15, 104.25) * mm});
            skCircle(sketch, "E82", {"center": v(0, 104.25) * mm, "radius": 6 * mm});
            skLineSegment(sketch, "E83", {"start": v(15, 92.25) * mm, "end": v(33, 74.25) * mm});
            skLineSegment(sketch, "E84", {"start": v(0, 74.25) * mm, "end": v(0, 104.25) * mm, "construction": true});
            skLineSegment(sketch, "E85", {"start": v(-15, 92.25) * mm, "end": v(-33.91, 74.25) * mm});
            skPoint(sketch, "E86.endSnap0", {"position": v(0, -74.25) * mm});
            skLineSegment(sketch, "E87", {"start": v(-74.25, 0) * mm, "end": v(74.25, 0) * mm, "construction": true});
            skLineSegment(sketch, "E88.MirrorCS", {"start": v(15, -92.25) * mm, "end": v(33, -74.25) * mm});
            skLineSegment(sketch, "E89.MirrorCS", {"start": v(15, -92.25) * mm, "end": v(15, -104.25) * mm});
            skArc(sketch, "E90.MirrorCS", {"start": v(15, -104.25) * mm, "mid": v(0, -119.25) * mm, "end": v(-15, -104.25) * mm});
            skCircle(sketch, "E91.MirrorC", {"center": v(0, -104.25) * mm, "radius": 6 * mm});
            skLineSegment(sketch, "E92.MirrorCS", {"start": v(-15, -92.25) * mm, "end": v(-15, -104.25) * mm});
            skLineSegment(sketch, "E93.MirrorCS", {"start": v(-15, -92.25) * mm, "end": v(-33.91, -74.25) * mm});
            skLineSegment(sketch, "E94.MirrorCS", {"start": v(0, -74.25) * mm, "end": v(0, -104.25) * mm, "construction": true});
            skSolve(sketch);
        }
        {
            var Q0;
            Q0=makeQuery(id+"F16.imprint","IMPRINT",FACE,{"disambiguationData":[TD([[makeQuery(id+"F16.imprint","IMPRINT",EDGE,{"derivedFrom":sQuery(id+"F16.wireOp",EDGE,"E79")}),-1.0]])]});
            var Q1;
            Q1=makeQuery(id+"F16.imprint","IMPRINT",FACE,{"disambiguationData":[TD([[makeQuery(id+"F16.imprint","IMPRINT",EDGE,{"derivedFrom":makeQuery(id+"F1.opExtrude","CAP_EDGE",EDGE,{"disambiguationData":[OSD([sQuery(id+"F0.wireOp",EDGE,"E1.left")])],"isStart":true})}),-1.0]])]});
            var Q2;
            {var subQ0=sQuery(id+"F16.wireOp",EDGE,"E88.MirrorCS");Q2=makeQuery(id+"F16.imprint","IMPRINT",FACE,{"disambiguationData":[TD([[makeQuery(id+"F16.imprint","IMPRINT",EDGE,{"derivedFrom":subQ0}),1.0]])]});}
            var Q3;
            Q3=makeQuery(id+"F2.opExtrude","CAP_FACE",FACE,{"disambiguationData":[OSD([sQuery(id+"F0.wireOp",EDGE,"E12"),sQuery(id+"F0.wireOp",EDGE,"E13"),sQuery(id+"F0.wireOp",EDGE,"E14"),sQuery(id+"F0.wireOp",EDGE,"E15"),sQuery(id+"F0.wireOp",EDGE,"E17.filletArc"),sQuery(id+"F0.wireOp",EDGE,"E18.filletArc"),sQuery(id+"F0.wireOp",EDGE,"E19.filletArc"),sQuery(id+"F0.wireOp",EDGE,"E20.filletArc"),sQuery(id+"F0.wireOp",EDGE,"E25.0"),sQuery(id+"F0.wireOp",EDGE,"E25.1"),sQuery(id+"F0.wireOp",EDGE,"E25.2"),sQuery(id+"F0.wireOp",EDGE,"E25.3"),sQuery(id+"F0.wireOp",EDGE,"E25.4"),sQuery(id+"F0.wireOp",EDGE,"E25.5"),sQuery(id+"F0.wireOp",EDGE,"E25.6"),sQuery(id+"F0.wireOp",EDGE,"E25.7")])],"isStart":false});
            extrude(context, id + "F17", {"entities" : qUnion([Q0, Q1, Q2]), "operationType" : NewBodyOperationType.ADD, "endBound" : BoundingType.UP_TO_SURFACE, "depth" : 25 * mm, "endBoundEntityFace" : qUnion([Q3]), "offsetDistance" : 25 * mm});
        }
    });
